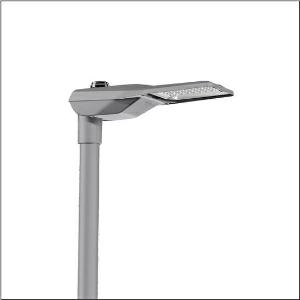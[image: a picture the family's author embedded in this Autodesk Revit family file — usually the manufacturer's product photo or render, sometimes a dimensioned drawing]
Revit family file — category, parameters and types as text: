
# Revit family: streetlight_sl_21_mini___st1_0a_5xe6d27n08hb_8446
name_source: partatom
category: Lighting Fixtures
units: mm (PartAtom-declared; Revit-internal decimal feet)

## family parameters
Cut with Voids When Loaded = No
Host = Face
Light Source = No
Part Type = Normal
Room Calculation Point = No
Round Connector Dimension = Use Diameter
Shared = No

## types (1)
- --- (1 x LED, 7490 lm, 66 W, 2200K)
    Apparent Load = 66 VA
    CIE Flux Codes = 37 72 97 100 100
    Color Rendering = 70
    Color Temperature = 2200K
    Default Elevation = 1800 mm
    Description = Streetlight SL 21 mini, mast luminaire, primary light control with lens, of PMMA, primary optical cover: cover, of toughened safety glass, transparent, light distribution: ST1.0a, light emission: direct distribution, primary light characteristic: asymmetric, installation type: side-entry, LED, 3G 1.5mm², High Power LED, rated luminous flux: 7.490lm, luminous efficacy: 114lm/W, light colour: 722, colour temperature: 2200K, control gear: NEMA (7pin), control: overheat protection, pre-setting: linear dimming characteristic, constant luminous flux control, time-dependent luminous flux control, flexible luminous flux parameterisation, mains connection: 230..240V, AC, 50/60Hz, connection cable pre-assembled, cable length: 8,5m, wiring characteristics: H07RN-F, start of lifetime: 66W, end of service life: 69W, reduction: 30W, luminaire housing, of diecast aluminium (EN AC-44300), powder-coated, SITECO metallic grey (DB 702S), corrosivity category C5 high according to DIN EN ISO 12944, multi-level sealing system, sealing non-destructively replaceable, inclination adjustable: 0°, 5°, 10°, 15°, length: 628mm, width: 235mm, height: 110mm, spigot size: 42mm (side-entry), mounting height: 4..8m, protection rating (complete): IP66, insulation class (complete): insulation class I (protective earthing), certification: CE, ENEC, ENEC+, VDE, impact resistance: IK10, permissible operating ambient temperature for outdoor applications: -40..+50°C, standard-compliant lighting for roads and squares, packaging unit: 1 piece

Light Distribution: ST1.0a
    Height = 110 mm
    Lamp = 1 x LED
    Lamp Light Flux = 7490 lm
    Lamp Power = 66 W
    Lamp count = 1
    Length = 625 mm
    Luminous efficacy = 113 lm/W
    Manufacturer = Siteco
    ModVariant = No
    Model = 5XE6D27N08HB
    Mounting Place = Pole
    Mounting Type = Pole top
    Number of Poles = 1
    OnlyDefault = Yes
    Power Factor = 1
    Product Name = Streetlight SL 21 mini | ST1.0a
    Product group = mast luminaire | pylon top
    ProductGroupID = 6100
    Protection Class = Protection class I
    Protection Degree = IP 66
    RLX_Detail_Level = 1
    RLX_Emergency_Light_Flux = 0 lm
    RLX_Emergency_Type = 0
    RLX_Emergency_Type_DB = No
    RlxData = <blob elided: 26109 chars, md5=ba31eebd>
    Socket = socket
    Standby Power = 0 W
    System Light Flux = 7490 lm
    System Power = 66 W
    Type Comments = factory setting: luminous flux: 100 % | dim-lin: 254 | 670 mA
    Type Image = l_1294379.jpg
    URL = http://relux.com
    VarID = @adj_137411
    Voltage = 0 V
    Weight = 0.00 kg
    Width = 234 mm

## geometry (parser evidence)
native form markers: Blend x4, Sweep x11
no freeform markers — native parametric forms only
